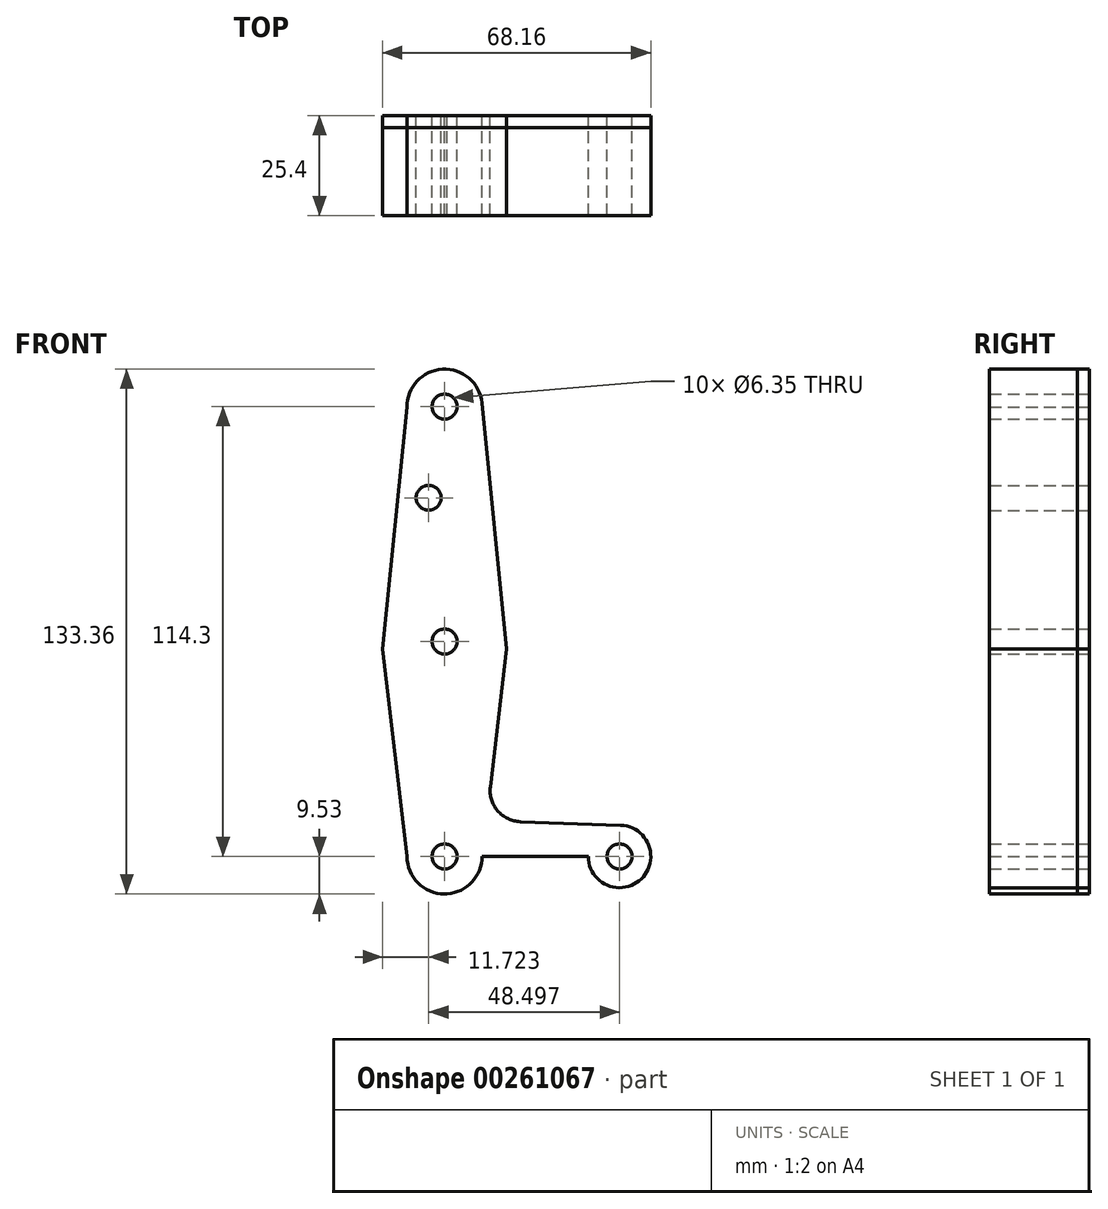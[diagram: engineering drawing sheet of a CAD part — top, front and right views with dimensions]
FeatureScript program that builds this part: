
annotation { "Feature Type Name" : "Feature", "Feature Type Description" : "" }
export const myFeature = defineFeature(function(context is Context, id is Id, definition is map)
    precondition{}
    {
        {
            var Q0;
            Q0=qCreatedBy(makeId("Front.planeOp"),FACE);
            var sketch = newSketch(context, id + "F0", { "sketchPlane" : qUnion([Q0])});
            skCircle(sketch, "E0", {"center": v(0, 114.3) * mm, "radius": 9.53 * mm});
            skCircle(sketch, "E1", {"center": v(0, 54.61) * mm, "radius": 15.88 * mm});
            skCircle(sketch, "E2", {"center": v(0, 0) * mm, "radius": 9.53 * mm});
            skCircle(sketch, "E3", {"center": v(44.45, 0) * mm, "radius": 7.94 * mm});
            skLineSegment(sketch, "E4", {"start": v(0, 114.3) * mm, "end": v(0, 0) * mm});
            skLineSegment(sketch, "E5", {"start": v(0, 0) * mm, "end": v(44.45, 0) * mm});
            skLineSegment(sketch, "E6", {"start": v(0, -9.53) * mm, "end": v(44.73, -7.93) * mm});
            skLineSegment(sketch, "E7", {"start": v(19.23, 8.84) * mm, "end": v(44.73, 7.93) * mm});
            skLineSegment(sketch, "E8", {"start": v(-9.52, 0) * mm, "end": v(-15.77, 52.74) * mm});
            skLineSegment(sketch, "E9", {"start": v(11.62, 17.72) * mm, "end": v(15.77, 52.74) * mm});
            skLineSegment(sketch, "E10", {"start": v(15.77, 52.74) * mm, "end": v(9.48, 115.25) * mm});
            skLineSegment(sketch, "E11", {"start": v(-9.52, 114.15) * mm, "end": v(-15.77, 52.74) * mm});
            skCircle(sketch, "E12", {"center": v(0, 114.3) * mm, "radius": 3.18 * mm});
            skCircle(sketch, "E13", {"center": v(0, 54.61) * mm, "radius": 3.18 * mm});
            skCircle(sketch, "E14", {"center": v(0, 0) * mm, "radius": 3.18 * mm});
            skCircle(sketch, "E15", {"center": v(44.45, 0) * mm, "radius": 3.18 * mm});
            skCircle(sketch, "E16", {"center": v(-4.05, 91.14) * mm, "radius": 3.18 * mm});
            skArc(sketch, "E17.filletArc", {"start": v(11.62, 17.72) * mm, "mid": v(13.48, 11.61) * mm, "end": v(19.23, 8.84) * mm});
            skSolve(sketch);
        }
        {
            var Q0;
            {var subQ0=sQuery(id+"F0.wireOp",EDGE,"E10");var subQ1=sQuery(id+"F0.wireOp",EDGE,"E0");var subQ2=makeQuery(id+"F0.imprint","INTERSECT",VERTEX,{"derivedFrom":[subQ1,subQ0]});Q0=makeQuery(id+"F0.imprint","IMPRINT",FACE,{"disambiguationData":[TD([[makeQuery(id+"F0.imprint","IMPRINT",EDGE,{"disambiguationData":[TD([[subQ2,1.0]])],"derivedFrom":subQ1}),-1.0]])]});}
            var Q1;
            Q1=makeQuery(id+"F0.imprint","IMPRINT",FACE,{"disambiguationData":[TD([[makeQuery(id+"F0.imprint","IMPRINT",EDGE,{"derivedFrom":sQuery(id+"F0.wireOp",EDGE,"E16")}),-1.0]])]});
            var Q2;
            Q2=makeQuery(id+"F0.imprint","IMPRINT",FACE,{"disambiguationData":[TD([[makeQuery(id+"F0.imprint","IMPRINT",EDGE,{"derivedFrom":sQuery(id+"F0.wireOp",EDGE,"E12")}),-1.0]])]});
            var Q3;
            {var subQ1=sQuery(id+"F0.wireOp",EDGE,"E1");var subQ5=sQuery(id+"F0.wireOp",EDGE,"E10");var subQ9=makeQuery(id+"F0.imprint","INTERSECT",VERTEX,{"derivedFrom":[subQ1,subQ5]});Q3=makeQuery(id+"F0.imprint","IMPRINT",FACE,{"disambiguationData":[TD([[makeQuery(id+"F0.imprint","IMPRINT",EDGE,{"disambiguationData":[TD([[subQ9,-1.0]])],"derivedFrom":subQ1}),1.0]])]});}
            var Q4;
            {var subQ1=sQuery(id+"F0.wireOp",EDGE,"E1");var subQ7=sQuery(id+"F0.wireOp",EDGE,"E11");var subQ9=makeQuery(id+"F0.imprint","INTERSECT",VERTEX,{"derivedFrom":[subQ1,subQ7]});Q4=makeQuery(id+"F0.imprint","IMPRINT",FACE,{"disambiguationData":[TD([[makeQuery(id+"F0.imprint","IMPRINT",EDGE,{"disambiguationData":[TD([[subQ9,1.0]])],"derivedFrom":subQ1}),1.0]])]});}
            var Q5;
            {var subQ0=sQuery(id+"F0.wireOp",EDGE,"E8");Q5=makeQuery(id+"F0.imprint","IMPRINT",FACE,{"disambiguationData":[TD([[makeQuery(id+"F0.imprint","IMPRINT",EDGE,{"derivedFrom":subQ0}),-1.0]])]});}
            var Q6;
            {var subQ0=sQuery(id+"F0.wireOp",EDGE,"E7");Q6=makeQuery(id+"F0.imprint","IMPRINT",FACE,{"disambiguationData":[TD([[makeQuery(id+"F0.imprint","IMPRINT",EDGE,{"derivedFrom":subQ0}),-1.0]])]});}
            var Q7;
            {var subQ0=sQuery(id+"F0.wireOp",EDGE,"E6");var subQ1=sQuery(id+"F0.wireOp",EDGE,"E2");var subQ2=makeQuery(id+"F0.imprint","INTERSECT",VERTEX,{"disambiguationData":[OD(1.0)],"derivedFrom":[subQ1,subQ0]});Q7=makeQuery(id+"F0.imprint","IMPRINT",FACE,{"disambiguationData":[TD([[makeQuery(id+"F0.imprint","IMPRINT",EDGE,{"disambiguationData":[TD([[subQ2,-1.0]])],"derivedFrom":subQ1}),-1.0]])]});}
            var Q8;
            {var subQ1=sQuery(id+"F0.wireOp",EDGE,"E2");var subQ11=makeQuery(id+"F0.imprint","INTERSECT",VERTEX,{"derivedFrom":[subQ1,sQuery(id+"F0.wireOp",EDGE,"E8")]});Q8=makeQuery(id+"F0.imprint","IMPRINT",FACE,{"disambiguationData":[TD([[makeQuery(id+"F0.imprint","IMPRINT",EDGE,{"disambiguationData":[TD([[subQ11,1.0]])],"derivedFrom":subQ1}),1.0]])]});}
            var Q9;
            {var subQ0=sQuery(id+"F0.wireOp",EDGE,"E4");var subQ1=sQuery(id+"F0.wireOp",EDGE,"E2");var subQ2=makeQuery(id+"F0.imprint","INTERSECT",VERTEX,{"derivedFrom":[subQ1,subQ0]});Q9=makeQuery(id+"F0.imprint","IMPRINT",FACE,{"disambiguationData":[TD([[makeQuery(id+"F0.imprint","IMPRINT",EDGE,{"disambiguationData":[TD([[subQ2,1.0]])],"derivedFrom":subQ1}),1.0]])]});}
            var Q10;
            Q10=makeQuery(id+"F0.imprint","IMPRINT",FACE,{"disambiguationData":[TD([[makeQuery(id+"F0.imprint","IMPRINT",EDGE,{"derivedFrom":sQuery(id+"F0.wireOp",EDGE,"E15")}),-1.0]])]});
            extrude(context, id + "F1", {"entities" : qUnion([Q0, Q1, Q2, Q3, Q4, Q5, Q6, Q7, Q8, Q9, Q10]), "depth" : 3.05 * mm});
        }
        {
            var Q0;
            {var subQ0=sQuery(id+"F0.wireOp",EDGE,"E6");var subQ1=sQuery(id+"F0.wireOp",EDGE,"E2");var subQ2=makeQuery(id+"F0.imprint","INTERSECT",VERTEX,{"disambiguationData":[OD(1.0)],"derivedFrom":[subQ1,subQ0]});Q0=makeQuery(id+"F0.imprint","IMPRINT",FACE,{"disambiguationData":[TD([[makeQuery(id+"F0.imprint","IMPRINT",EDGE,{"disambiguationData":[TD([[subQ2,-1.0]])],"derivedFrom":subQ1}),-1.0]])]});}
            var Q1;
            {var subQ1=sQuery(id+"F0.wireOp",EDGE,"E2");var subQ11=makeQuery(id+"F0.imprint","INTERSECT",VERTEX,{"derivedFrom":[subQ1,sQuery(id+"F0.wireOp",EDGE,"E8")]});Q1=makeQuery(id+"F0.imprint","IMPRINT",FACE,{"disambiguationData":[TD([[makeQuery(id+"F0.imprint","IMPRINT",EDGE,{"disambiguationData":[TD([[subQ11,1.0]])],"derivedFrom":subQ1}),1.0]])]});}
            var Q2;
            {var subQ0=sQuery(id+"F0.wireOp",EDGE,"E7");Q2=makeQuery(id+"F0.imprint","IMPRINT",FACE,{"disambiguationData":[TD([[makeQuery(id+"F0.imprint","IMPRINT",EDGE,{"derivedFrom":subQ0}),-1.0]])]});}
            var Q3;
            {var subQ0=sQuery(id+"F0.wireOp",EDGE,"E4");var subQ1=sQuery(id+"F0.wireOp",EDGE,"E2");var subQ2=makeQuery(id+"F0.imprint","INTERSECT",VERTEX,{"derivedFrom":[subQ1,subQ0]});Q3=makeQuery(id+"F0.imprint","IMPRINT",FACE,{"disambiguationData":[TD([[makeQuery(id+"F0.imprint","IMPRINT",EDGE,{"disambiguationData":[TD([[subQ2,1.0]])],"derivedFrom":subQ1}),1.0]])]});}
            var Q4;
            {var subQ0=sQuery(id+"F0.wireOp",EDGE,"E8");Q4=makeQuery(id+"F0.imprint","IMPRINT",FACE,{"disambiguationData":[TD([[makeQuery(id+"F0.imprint","IMPRINT",EDGE,{"derivedFrom":subQ0}),-1.0]])]});}
            var Q5;
            {var subQ1=sQuery(id+"F0.wireOp",EDGE,"E1");var subQ7=sQuery(id+"F0.wireOp",EDGE,"E11");var subQ9=makeQuery(id+"F0.imprint","INTERSECT",VERTEX,{"derivedFrom":[subQ1,subQ7]});Q5=makeQuery(id+"F0.imprint","IMPRINT",FACE,{"disambiguationData":[TD([[makeQuery(id+"F0.imprint","IMPRINT",EDGE,{"disambiguationData":[TD([[subQ9,1.0]])],"derivedFrom":subQ1}),1.0]])]});}
            var Q6;
            {var subQ1=sQuery(id+"F0.wireOp",EDGE,"E1");var subQ5=sQuery(id+"F0.wireOp",EDGE,"E10");var subQ9=makeQuery(id+"F0.imprint","INTERSECT",VERTEX,{"derivedFrom":[subQ1,subQ5]});Q6=makeQuery(id+"F0.imprint","IMPRINT",FACE,{"disambiguationData":[TD([[makeQuery(id+"F0.imprint","IMPRINT",EDGE,{"disambiguationData":[TD([[subQ9,-1.0]])],"derivedFrom":subQ1}),1.0]])]});}
            var Q7;
            {var subQ0=sQuery(id+"F0.wireOp",EDGE,"E10");var subQ1=sQuery(id+"F0.wireOp",EDGE,"E0");var subQ2=makeQuery(id+"F0.imprint","INTERSECT",VERTEX,{"derivedFrom":[subQ1,subQ0]});Q7=makeQuery(id+"F0.imprint","IMPRINT",FACE,{"disambiguationData":[TD([[makeQuery(id+"F0.imprint","IMPRINT",EDGE,{"disambiguationData":[TD([[subQ2,1.0]])],"derivedFrom":subQ1}),-1.0]])]});}
            var Q8;
            Q8=makeQuery(id+"F0.imprint","IMPRINT",FACE,{"disambiguationData":[TD([[makeQuery(id+"F0.imprint","IMPRINT",EDGE,{"derivedFrom":sQuery(id+"F0.wireOp",EDGE,"E16")}),-1.0]])]});
            var Q9;
            Q9=makeQuery(id+"F0.imprint","IMPRINT",FACE,{"disambiguationData":[TD([[makeQuery(id+"F0.imprint","IMPRINT",EDGE,{"derivedFrom":sQuery(id+"F0.wireOp",EDGE,"E15")}),-1.0]])]});
            var Q10;
            Q10=makeQuery(id+"F0.imprint","IMPRINT",FACE,{"disambiguationData":[TD([[makeQuery(id+"F0.imprint","IMPRINT",EDGE,{"derivedFrom":sQuery(id+"F0.wireOp",EDGE,"E12")}),-1.0]])]});
            extrude(context, id + "F2", {"entities" : qUnion([Q0, Q1, Q2, Q3, Q4, Q5, Q6, Q7, Q8, Q9, Q10]), "depth" : 25.4 * mm});
        }
    });
